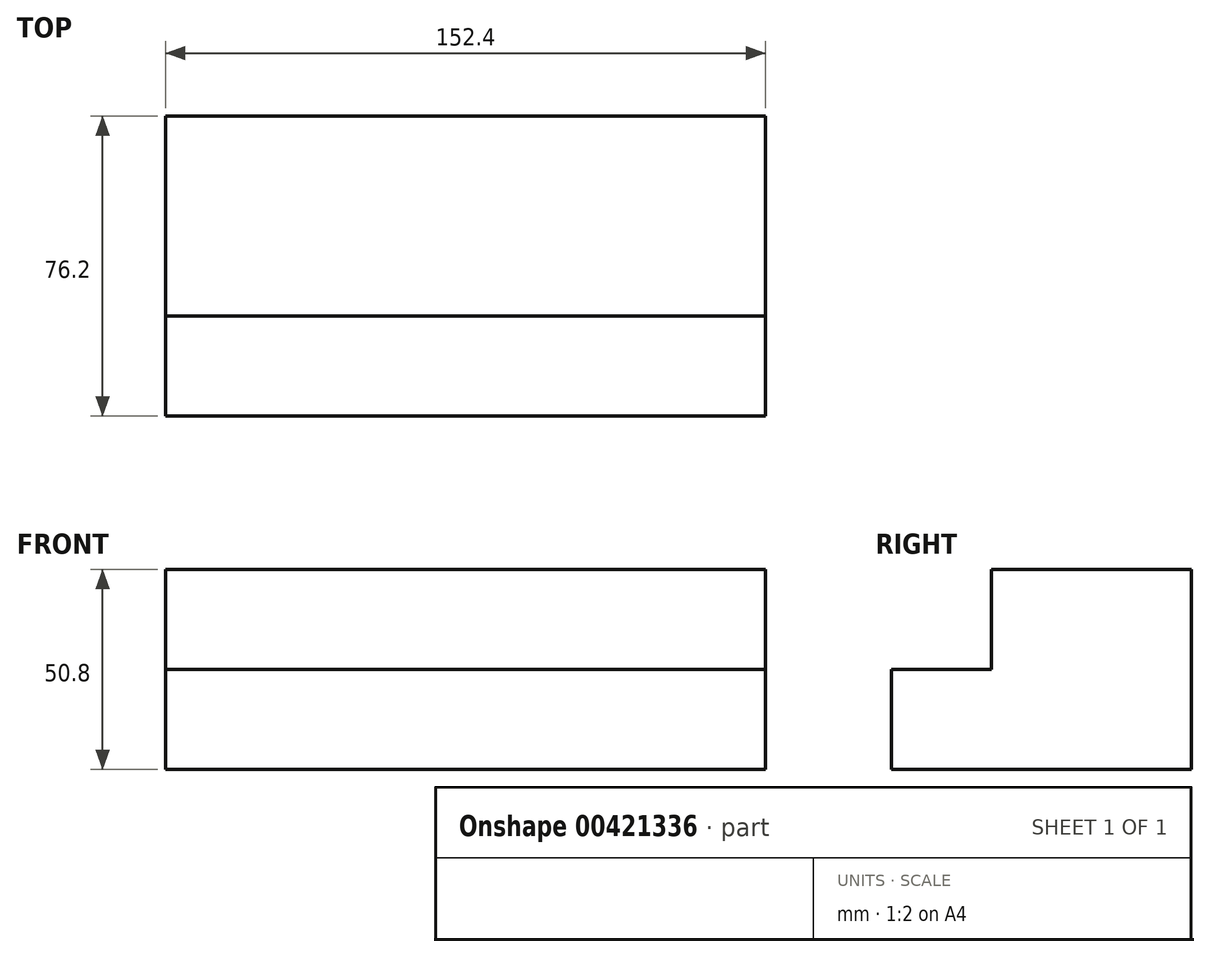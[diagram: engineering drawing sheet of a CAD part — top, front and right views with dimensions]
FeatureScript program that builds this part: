
annotation { "Feature Type Name" : "Feature", "Feature Type Description" : "" }
export const myFeature = defineFeature(function(context is Context, id is Id, definition is map)
    precondition{}
    {
        {
            var Q0;
            Q0=qCreatedBy(makeId("Right.planeOp"),FACE);
            var sketch = newSketch(context, id + "F0", { "sketchPlane" : qUnion([Q0])});
            skLineSegment(sketch, "E0", {"start": v(0, 0) * mm, "end": v(0, 25.4) * mm});
            skLineSegment(sketch, "E1", {"start": v(0, 25.4) * mm, "end": v(25.4, 25.4) * mm});
            skLineSegment(sketch, "E2", {"start": v(25.4, 25.4) * mm, "end": v(25.4, 50.8) * mm});
            skLineSegment(sketch, "E3", {"start": v(25.4, 50.8) * mm, "end": v(76.2, 50.8) * mm});
            skLineSegment(sketch, "E4", {"start": v(76.2, 50.8) * mm, "end": v(76.2, 0) * mm});
            skLineSegment(sketch, "E5", {"start": v(0, 0) * mm, "end": v(76.2, 0) * mm});
            skSolve(sketch);
        }
        {
            var Q0;
            Q0=makeQuery(id+"F0.imprint","IMPRINT",FACE,{"disambiguationData":[TD([[makeQuery(id+"F0.imprint","IMPRINT",EDGE,{"derivedFrom":sQuery(id+"F0.wireOp",EDGE,"E0")}),-1.0]])]});
            extrude(context, id + "F1", {"entities" : qUnion([Q0]), "depth" : 152.4 * mm});
        }
    });
